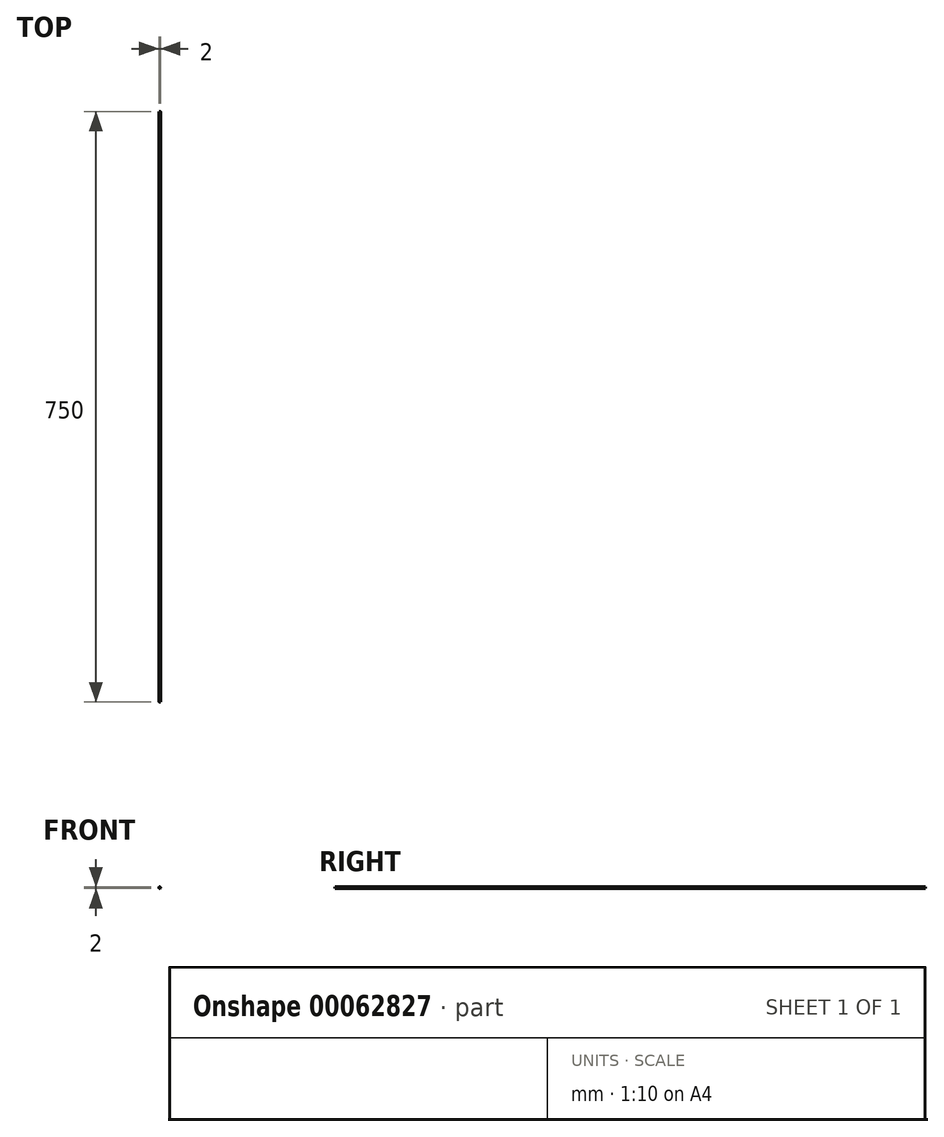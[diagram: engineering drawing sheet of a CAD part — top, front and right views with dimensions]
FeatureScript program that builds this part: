
annotation { "Feature Type Name" : "Feature", "Feature Type Description" : "" }
export const myFeature = defineFeature(function(context is Context, id is Id, definition is map)
    precondition{}
    {
        {
            var Q0;
            Q0=qCreatedBy(makeId("Front.planeOp"),FACE);
            var sketch = newSketch(context, id + "F0", { "sketchPlane" : qUnion([Q0])});
            skCircle(sketch, "E0", {"center": v(0, 0) * mm, "radius": 1 * mm});
            skSolve(sketch);
        }
        {
            var Q0;
            Q0=qCreatedBy(makeId("Right.planeOp"),FACE);
            var sketch = newSketch(context, id + "F1", { "sketchPlane" : qUnion([Q0])});
            skLineSegment(sketch, "E1", {"start": v(0, 0) * mm, "end": v(-750, 0) * mm});
            skSolve(sketch);
        }
        {
            var Q0;
            Q0 = qSketchRegion(id + "F0", true);
            var Q1;
            Q1 = qConstructionFilter(qBodyType(qCreatedBy(id + "F1" ,EDGE), BodyType.WIRE), ConstructionObject.NO);
            sweep(context, id + "F2", {"profiles" : qUnion([Q0]), "path" : qUnion([Q1])});
        }
        {
            var Q0;
            Q0=makeQuery(id+"F2.opSweep","CAP_FACE",FACE,{"disambiguationData":[OSD([sQuery(id+"F0.wireOp",EDGE,"E0"),sQuery(id+"F1.wireOp",VERTEX,"E1.end")])],"isStart":false});
            var sketch = newSketch(context, id + "F3", { "sketchPlane" : qUnion([Q0])});
            skLineSegment(sketch, "E2", {"start": v(0, -1) * mm, "end": v(4.51, -1) * mm, "construction": true});
            skSolve(sketch);
        }
    });
